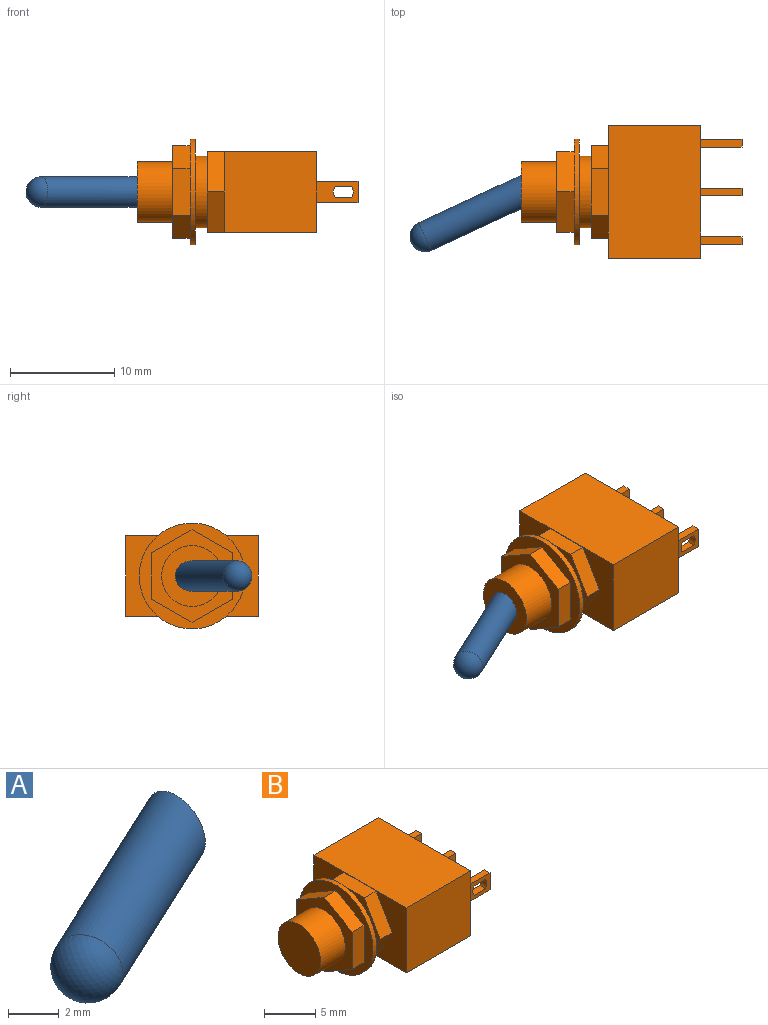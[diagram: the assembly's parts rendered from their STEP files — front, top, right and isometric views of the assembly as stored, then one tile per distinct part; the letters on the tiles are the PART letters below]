
ASSEMBLY  parts=2 mates=1
PART A: 3 faces, bbox 11.9x7.4x2.9 mm
  f0: plane 3.22x2.92mm, normal (1,0,0), area 7.4mm2, adj f1
  f1: cylinder r=1.46mm len=11.06mm, axis (0.91,0.42,0), area 93.2mm2, adj f0,f2
  f2: sphere r=1.46mm, area 13.4mm2, adj f1
PART B: 53 faces, bbox 21.2x12.7x10.2 mm
  f0: plane 12.7x8.89mm, normal (0,0,1), area 112.9mm2, adj f5,f6,f7,f8
  f1: plane 12.7x8.89mm, normal (0,0,-1), area 112.9mm2, adj f5,f6,f7,f8
  f2: cylinder r=3.43mm len=6.86mm, axis (1,0,0), area 24.6mm2, adj f39,f45
  f3: cylinder r=2.92mm len=5.84mm, axis (1,0,0), area 63.1mm2, adj f4,f46
  f4: plane 5.84x5.84mm, normal (-1,0,0), area 26.8mm2, adj f3
  f5: plane 12.7x7.75mm, normal (-1,0,0), area 47.1mm2, adj f0,f1,f6,f7,f33,f34,f35,f36
  f6: plane 8.89x7.75mm, normal (0,1,0), area 68.9mm2, adj f0,f1,f5,f8
  f7: plane 8.89x7.75mm, normal (0,-1,0), area 68.9mm2, adj f0,f1,f5,f8
  f8: plane 12.7x7.75mm, normal (1,0,0), area 93.8mm2, adj f0,f1,f6,f7,f9,f10,f11,f12
  f9: plane 3.94x2.03mm, normal (0,-1,0), area 6mm2, adj f8,f10,f12,f21,f22,f23,f24,f42
  f10: plane 3.94x0.76mm, normal (0,0,1), area 3mm2, adj f8,f9,f11,f24
  f11: plane 3.94x2.03mm, normal (0,1,0), area 6mm2, adj f8,f10,f12,f21,f22,f23,f24,f42
  f12: plane 3.94x0.76mm, normal (0,0,-1), area 3mm2, adj f8,f9,f11,f24
  f13: plane 3.94x2.03mm, normal (0,-1,0), area 6mm2, adj f8,f14,f16,f25,f26,f27,f28,f41
  f14: plane 3.94x0.76mm, normal (0,0,1), area 3mm2, adj f8,f13,f15,f28
  f15: plane 3.94x2.03mm, normal (0,1,0), area 6mm2, adj f8,f14,f16,f25,f26,f27,f28,f41
  f16: plane 3.94x0.76mm, normal (0,0,-1), area 3mm2, adj f8,f13,f15,f28
  f17: plane 3.94x2.03mm, normal (0,-1,0), area 6mm2, adj f8,f18,f20,f29,f30,f31,f32,f40
  f18: plane 3.94x0.76mm, normal (0,0,1), area 3mm2, adj f8,f17,f19,f32
  f19: plane 3.94x2.03mm, normal (0,1,0), area 6mm2, adj f8,f18,f20,f29,f30,f31,f32,f40
  f20: plane 3.94x0.76mm, normal (0,0,-1), area 3mm2, adj f8,f17,f19,f32
  f21: plane 1.57x0.76mm, normal (0,0,-1), area 1.2mm2, adj f9,f11,f23,f42
  f22: plane 1.57x0.76mm, normal (0,0,1), area 1.2mm2, adj f9,f11,f23,f42
  f23: cylinder r=1.02mm len=1.12mm, axis (0,-1,0), area 0.9mm2, adj f9,f11,f21,f22
  f24: plane 2.03x0.76mm, normal (1,0,0), area 1.5mm2, adj f9,f10,f11,f12
  f25: plane 1.57x0.76mm, normal (0,0,-1), area 1.2mm2, adj f13,f15,f27,f41
  f26: plane 1.57x0.76mm, normal (0,0,1), area 1.2mm2, adj f13,f15,f27,f41
  f27: cylinder r=1.02mm len=1.12mm, axis (0,-1,0), area 0.9mm2, adj f13,f15,f25,f26
  f28: plane 2.03x0.76mm, normal (1,0,0), area 1.5mm2, adj f13,f14,f15,f16
  f29: plane 1.57x0.76mm, normal (0,0,-1), area 1.2mm2, adj f17,f19,f31,f40
  f30: plane 1.57x0.76mm, normal (0,0,1), area 1.2mm2, adj f17,f19,f31,f40
  f31: cylinder r=1.02mm len=1.12mm, axis (0,-1,0), area 0.9mm2, adj f17,f19,f29,f30
  f32: plane 2.03x0.76mm, normal (1,0,0), area 1.5mm2, adj f17,f18,f19,f20
  f33: plane 4.44x1.65mm, normal (0,0,1), area 7.3mm2, adj f5,f34,f38,f39
  f34: plane 3.85x2.22mm, normal (0,-0.87,0.5), area 7.3mm2, adj f5,f33,f35,f39
  f35: plane 3.85x2.22mm, normal (0,-0.87,-0.5), area 7.3mm2, adj f5,f34,f36,f39
  f36: plane 4.44x1.65mm, normal (0,0,-1), area 7.3mm2, adj f5,f35,f37,f39
  f37: plane 3.85x2.22mm, normal (0,0.87,-0.5), area 7.3mm2, adj f5,f36,f38,f39
  f38: plane 3.85x2.22mm, normal (0,0.87,0.5), area 7.3mm2, adj f5,f33,f37,f39
  f39: plane 8.89x7.7mm, normal (-1,0,0), area 14.3mm2, adj f2,f33,f34,f35,f36,f37,f38
  f40: cylinder r=1.02mm len=1.12mm, axis (0,-1,0), area 0.9mm2, adj f17,f19,f29,f30
  f41: cylinder r=1.02mm len=1.12mm, axis (0,-1,0), area 0.9mm2, adj f13,f15,f25,f26
  f42: cylinder r=1.02mm len=1.12mm, axis (0,-1,0), area 0.9mm2, adj f9,f11,f21,f22
  f43: cylinder r=5.08mm len=10.16mm, axis (1,0,0), area 16.2mm2, adj f44,f45
  f44: plane 10.16x10.16mm, normal (-1,0,0), area 29.8mm2, adj f43,f47,f48,f49,f50,f51,f52
  f45: plane 10.16x10.16mm, normal (1,0,0), area 44.1mm2, adj f2,f43
  f46: plane 8.89x7.7mm, normal (-1,0,0), area 24.5mm2, adj f3,f47,f48,f49,f50,f51,f52
  f47: plane 3.85x2.22mm, normal (0,-0.5,0.87), area 7.3mm2, adj f44,f46,f48,f52
  f48: plane 3.85x2.22mm, normal (0,0.5,0.87), area 7.3mm2, adj f44,f46,f47,f49
  f49: plane 4.44x1.65mm, normal (0,1,0), area 7.3mm2, adj f44,f46,f48,f50
  f50: plane 3.85x2.22mm, normal (0,0.5,-0.87), area 7.3mm2, adj f44,f46,f49,f51
  f51: plane 3.85x2.22mm, normal (0,-0.5,-0.87), area 7.3mm2, adj f44,f46,f50,f52
  f52: plane 4.44x1.65mm, normal (0,-1,0), area 7.3mm2, adj f44,f46,f47,f51
PLACE A t=(0.5,0.61,0)mm
PLACE B at identity fixed
MATE fastened B.f3 <-> A.f0  axis (-1,0,0) through (-8.39,0,0)mm
